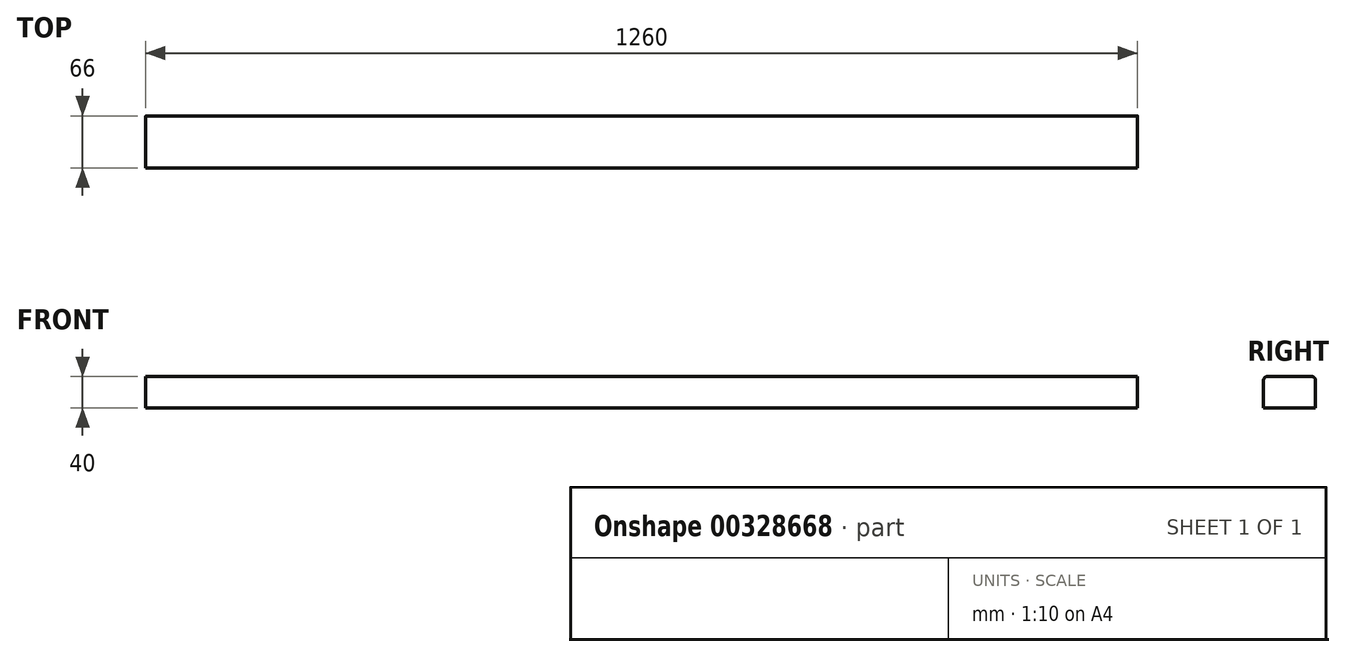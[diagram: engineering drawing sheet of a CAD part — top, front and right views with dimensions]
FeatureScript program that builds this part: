
annotation { "Feature Type Name" : "Feature", "Feature Type Description" : "" }
export const myFeature = defineFeature(function(context is Context, id is Id, definition is map)
    precondition{}
    {
        {
            var Q0;
            Q0=qCreatedBy(makeId("Right.planeOp"),FACE);
            var sketch = newSketch(context, id + "F0", { "sketchPlane" : qUnion([Q0])});
            skLineSegment(sketch, "E0.bottom", {"start": v(0, 0) * mm, "end": v(66, 0) * mm});
            skLineSegment(sketch, "E0.top", {"start": v(0, 40) * mm, "end": v(66, 40) * mm});
            skLineSegment(sketch, "E0.left", {"start": v(0, 0) * mm, "end": v(0, 40) * mm});
            skLineSegment(sketch, "E0.right", {"start": v(66, 0) * mm, "end": v(66, 40) * mm});
            skSolve(sketch);
        }
        {
            var Q0;
            Q0=makeQuery(id+"F0.imprint","IMPRINT",FACE,{"disambiguationData":[TD([[makeQuery(id+"F0.imprint","IMPRINT",EDGE,{"derivedFrom":sQuery(id+"F0.wireOp",EDGE,"E0.bottom")}),1.0]])]});
            extrude(context, id + "F1", {"entities" : qUnion([Q0]), "oppositeDirection" : true, "depth" : 1260 * mm});
        }
        {
            var Q0;
            Q0=makeQuery(id+"F1.opExtrude","SWEPT_EDGE",EDGE,{"disambiguationData":[OSD([sQuery(id+"F0.wireOp",EDGE,"E0.top"),sQuery(id+"F0.wireOp",EDGE,"E0.left")])]});
            var Q1;
            Q1=makeQuery(id+"F1.opExtrude","SWEPT_EDGE",EDGE,{"disambiguationData":[OSD([sQuery(id+"F0.wireOp",EDGE,"E0.top"),sQuery(id+"F0.wireOp",EDGE,"E0.right")])]});
            fillet(context, id + "F2", {"entities" : qUnion([Q0, Q1]), "radius" : 5 * mm, "tangentPropagation" : true, "allowEdgeOverflow" : false});
        }
    });
